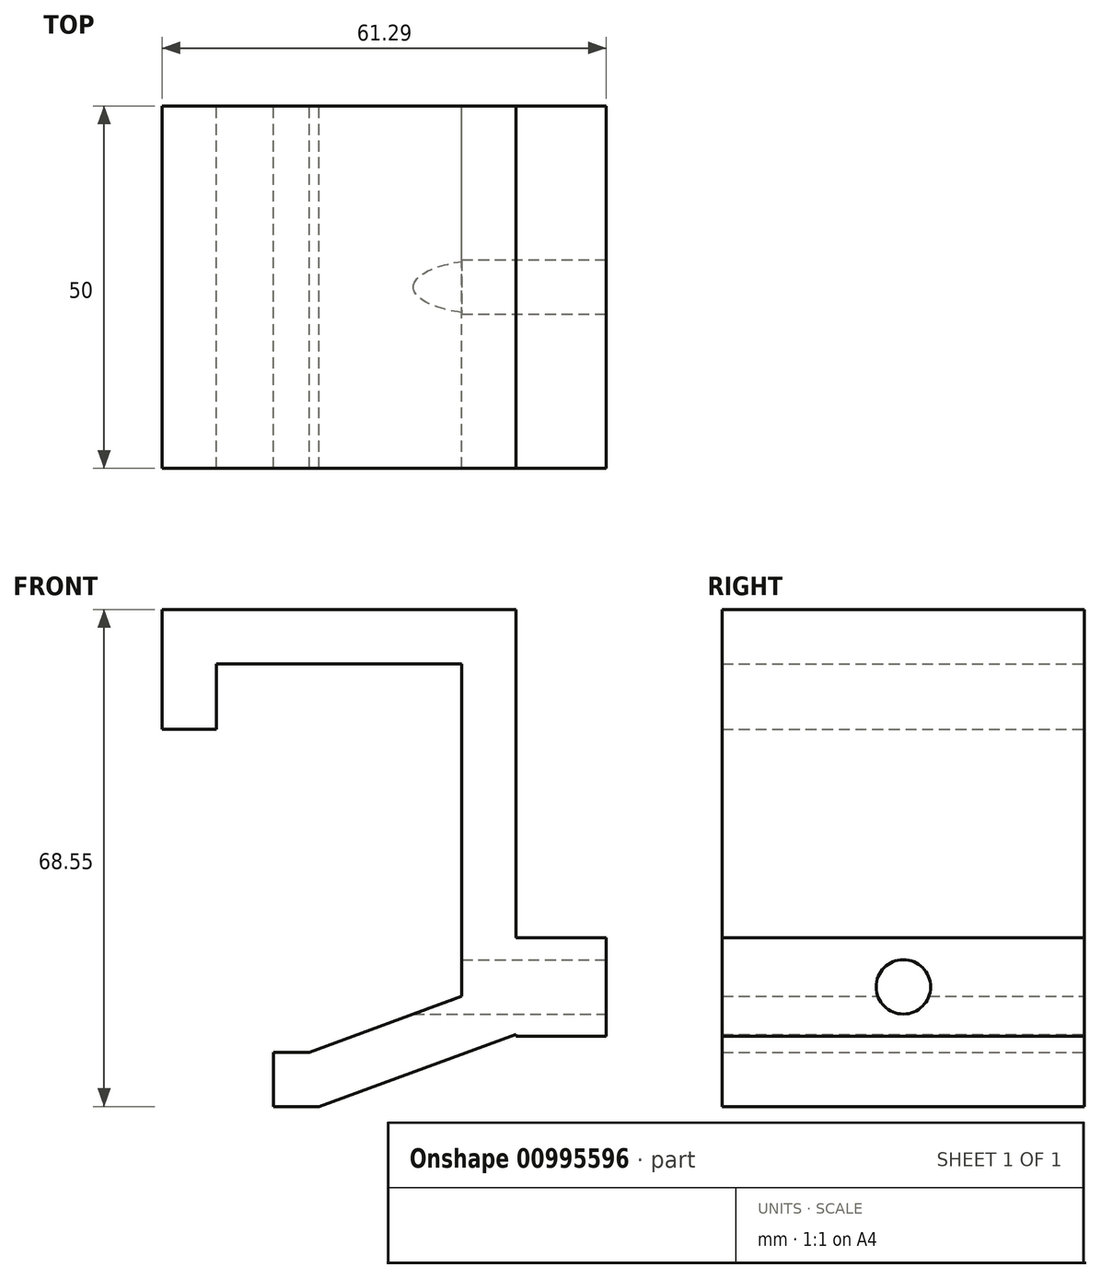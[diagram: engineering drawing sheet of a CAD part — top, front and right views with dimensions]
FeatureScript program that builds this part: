
annotation { "Feature Type Name" : "Feature", "Feature Type Description" : "" }
export const myFeature = defineFeature(function(context is Context, id is Id, definition is map)
    precondition{}
    {
        {
            var Q0;
            Q0=qCreatedBy(makeId("Front.planeOp"),FACE);
            var sketch = newSketch(context, id + "F0", { "sketchPlane" : qUnion([Q0])});
            skLineSegment(sketch, "E0", {"start": v(-33.84, 36.87) * mm, "end": v(-33.84, 45.85) * mm});
            skLineSegment(sketch, "E1", {"start": v(-33.84, 45.85) * mm, "end": v(0, 45.85) * mm});
            skLineSegment(sketch, "E2", {"start": v(0, 45.85) * mm, "end": v(0, 0) * mm});
            skLineSegment(sketch, "E3", {"start": v(0, 0) * mm, "end": v(-21, -7.7) * mm});
            skLineSegment(sketch, "E4", {"start": v(-21, -7.7) * mm, "end": v(-26, -7.7) * mm});
            skLineSegment(sketch, "E5.0", {"start": v(-19.66, -15.2) * mm, "end": v(-26, -15.2) * mm});
            skLineSegment(sketch, "E5.1", {"start": v(-41.34, 36.87) * mm, "end": v(-41.34, 53.35) * mm});
            skLineSegment(sketch, "E5.2", {"start": v(-41.34, 53.35) * mm, "end": v(7.5, 53.35) * mm});
            skLineSegment(sketch, "E5.3", {"start": v(7.5, 53.35) * mm, "end": v(7.5, -5.24) * mm});
            skLineSegment(sketch, "E5.4", {"start": v(7.5, -5.24) * mm, "end": v(-19.66, -15.2) * mm});
            skLineSegment(sketch, "E6", {"start": v(-41.34, 36.87) * mm, "end": v(-33.84, 36.87) * mm});
            skLineSegment(sketch, "E7", {"start": v(-26, -7.7) * mm, "end": v(-26, -15.2) * mm});
            skLineSegment(sketch, "E8.bottom", {"start": v(7.5, 8.1) * mm, "end": v(19.95, 8.1) * mm});
            skLineSegment(sketch, "E8.top", {"start": v(7.5, -5.49) * mm, "end": v(19.95, -5.49) * mm});
            skLineSegment(sketch, "E8.left", {"start": v(7.5, 8.1) * mm, "end": v(7.5, -5.49) * mm});
            skLineSegment(sketch, "E8.right", {"start": v(19.95, 8.1) * mm, "end": v(19.95, -5.49) * mm});
            skSolve(sketch);
        }
        {
            var Q0;
            Q0=makeQuery(id+"F0.imprint","IMPRINT",FACE,{"disambiguationData":[TD([[makeQuery(id+"F0.imprint","IMPRINT",EDGE,{"derivedFrom":sQuery(id+"F0.wireOp",EDGE,"E0")}),1.0]])]});
            var Q1;
            {var subQ3=sQuery(id+"F0.wireOp",EDGE,"E8.bottom");Q1=makeQuery(id+"F0.imprint","IMPRINT",FACE,{"disambiguationData":[TD([[makeQuery(id+"F0.imprint","IMPRINT",EDGE,{"derivedFrom":subQ3}),-1.0]])]});}
            extrude(context, id + "F1", {"entities" : qUnion([Q0, Q1]), "depth" : 50 * mm, "offsetDistance" : 25 * mm});
        }
        {
            var Q0;
            Q0=makeQuery(id+"F1.opExtrude","SWEPT_FACE",FACE,{"disambiguationData":[OSD([sQuery(id+"F0.wireOp",EDGE,"E8.right")])]});
            var sketch = newSketch(context, id + "F2", { "sketchPlane" : qUnion([Q0])});
            skLineSegment(sketch, "E9", {"start": v(-50, 1.3) * mm, "end": v(0, 1.3) * mm, "construction": true});
            skLineSegment(sketch, "E10", {"start": v(-25, 8.1) * mm, "end": v(-25, -5.49) * mm, "construction": true});
            skCircle(sketch, "E11", {"center": v(-25, 1.3) * mm, "radius": 3.75 * mm});
            skSolve(sketch);
        }
        {
            var Q0;
            Q0=makeQuery(id+"F2.imprint","IMPRINT",FACE,{"disambiguationData":[TD([[makeQuery(id+"F2.imprint","IMPRINT",EDGE,{"derivedFrom":sQuery(id+"F2.wireOp",EDGE,"E11")}),1.0]])]});
            extrude(context, id + "F3", {"entities" : qUnion([Q0]), "operationType" : NewBodyOperationType.REMOVE, "endBound" : BoundingType.THROUGH_ALL, "oppositeDirection" : true, "depth" : 25 * mm, "offsetDistance" : 25 * mm});
        }
    });
